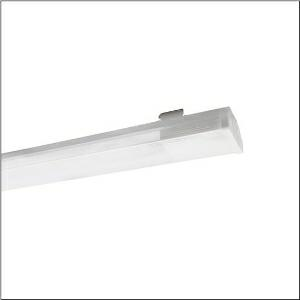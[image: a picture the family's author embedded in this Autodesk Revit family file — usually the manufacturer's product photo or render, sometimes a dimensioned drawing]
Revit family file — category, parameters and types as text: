
# Revit family: modario_31_gen_2_53bm812du4hxd2_9d50
name_source: partatom
category: Lighting Fixtures
units: mm (PartAtom-declared; Revit-internal decimal feet)

## family parameters
Cut with Voids When Loaded = No
Host = Face
Light Source = No
Part Type = Normal
Room Calculation Point = No
Round Connector Dimension = Use Diameter
Shared = No

## types (1)
- --- (1 x LED, 17250 lm, 92.2 W, 4000K)
    Apparent Load = 92 VA
    CIE Flux Codes = 47 80 95 93 100
    Color Rendering = 80
    Color Temperature = 4000K
    Default Elevation = 1800 mm
    Description = Modario 31 Gen.2, luminaire insert, of sheet steel, coil coated, white, length: 2.392mm, width: 81mm, height: 82mm, 8x system unit, system units: 299mm, LED rated luminous flux: 17.250lm, light colour: 840, SDCM (Standard Deviation of Colour Matching)MacAdam ≤ 3 SDCM (initial), control gear: DALI 2, control gear: ECG DALI, with plug, 5-pole, with phase selection, mains connection: 220..240V, AC, 50/60Hz, rated input power: 92W, through-wiring accessed according to module size, primary optical cover: cover, of PMMA, light emission: direct distribution, primary light characteristic: symmetric, protection rating (complete): IP20, protection rating (LED compartment): IP50, insulation class (complete): insulation class I (protective earthing), certification: CE, ENEC, VDE, UKCA, impact resistance: IK03, permissible ambient temperature for indoor applications: -25..+35°C, corresponds to IFS (International Featured Standards) requirements for safety and quality in the food industry, reducing of maximum allowable ambient temperature of 5°C with ceiling mounting, IP40 when using the optional accessory 5TP9018, packaging unit: 1 piece
    Height = 92 mm
    Lamp = 1 x LED
    Lamp Light Flux = 17250 lm
    Lamp Power = 92.2 W
    Lamp count = 1
    Length = 2392 mm
    Luminous efficacy = 187 lm/W
    Manufacturer = Siteco
    ModVariant = No
    Model = 53BM812DU4HXD2
    Mounting Place = Ceiling
    Mounting Type = Pendant
    Number of Poles = 1
    OnlyDefault = Yes
    Power Factor = 1
    Product Name = Modario 31 Gen.2
    Product group = luminaire insert | ceiling pendant
    ProductGroupID = 901
    Protection Class = Protection class I
    Protection Degree = IP 20
    RLX_Detail_Level = 1
    RLX_Emergency_Light_Flux = 0 lm
    RLX_Emergency_Type = 0
    RLX_Emergency_Type_DB = No
    RlxData = <blob elided: 38449 chars, md5=7cdfbe70>
    Socket = socket
    Standby Power = 0 W
    System Light Flux = 17250 lm
    System Power = 92 W
    Type Comments = factory setting: luminous flux: 100 % | dim-lin: 254 | 425 mA
    Type Image = l_1341883.jpg
    URL = http://relux.com
    VarID = @adj_050935
    Voltage = 0 V
    Weight = 0.00 kg
    Width = 81 mm

## geometry (parser evidence)
native form markers: Blend x4, Sweep x11
no freeform markers — native parametric forms only
